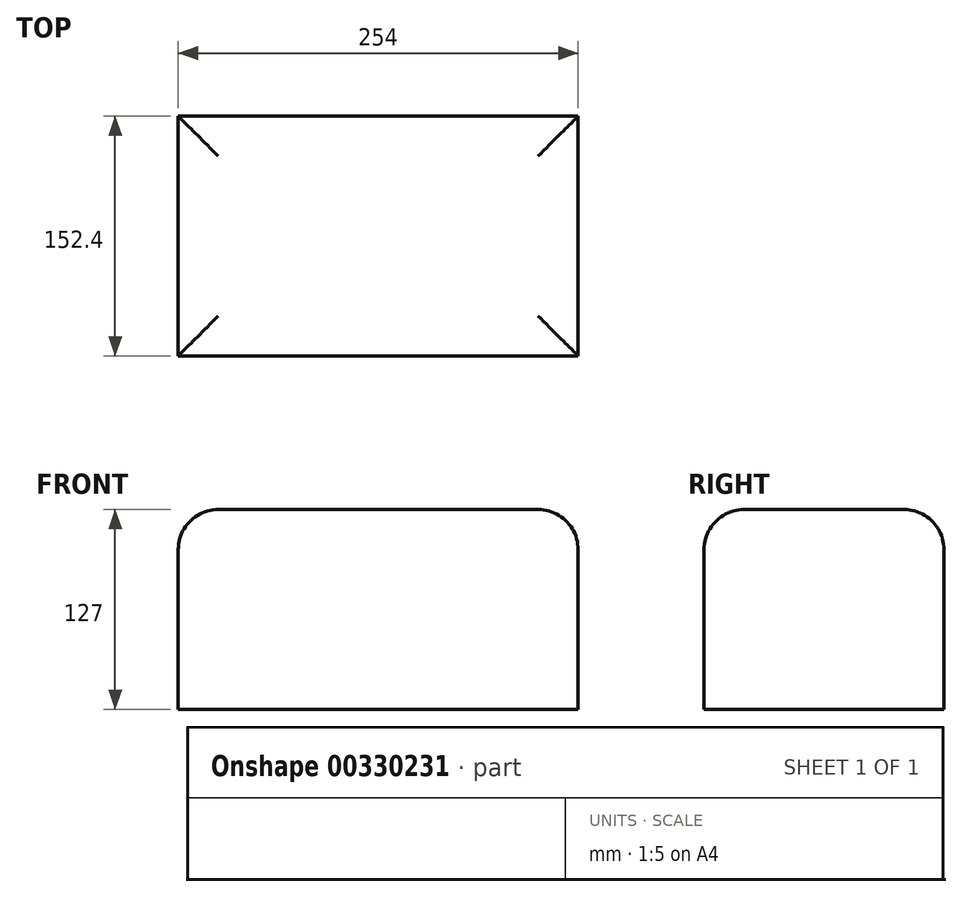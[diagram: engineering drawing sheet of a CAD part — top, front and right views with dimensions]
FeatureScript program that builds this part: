
annotation { "Feature Type Name" : "Feature", "Feature Type Description" : "" }
export const myFeature = defineFeature(function(context is Context, id is Id, definition is map)
    precondition{}
    {
        {
            var Q0;
            Q0=qCreatedBy(makeId("Top.planeOp"),FACE);
            var sketch = newSketch(context, id + "F0", { "sketchPlane" : qUnion([Q0])});
            skLineSegment(sketch, "E0.bottom", {"start": v(0, 0) * mm, "end": v(254, 0) * mm});
            skLineSegment(sketch, "E0.top", {"start": v(0, 152.4) * mm, "end": v(254, 152.4) * mm});
            skLineSegment(sketch, "E0.left", {"start": v(0, 0) * mm, "end": v(0, 152.4) * mm});
            skLineSegment(sketch, "E0.right", {"start": v(254, 0) * mm, "end": v(254, 152.4) * mm});
            skSolve(sketch);
        }
        {
            var Q0;
            Q0=makeQuery(id+"F0.imprint","IMPRINT",FACE,{"disambiguationData":[TD([[makeQuery(id+"F0.imprint","IMPRINT",EDGE,{"derivedFrom":sQuery(id+"F0.wireOp",EDGE,"E0.bottom")}),1.0]])]});
            extrude(context, id + "F1", {"entities" : qUnion([Q0]), "depth" : 127 * mm});
        }
        {
            var Q0;
            Q0=makeQuery(id+"F1.opExtrude","CAP_FACE",FACE,{"disambiguationData":[OSD([sQuery(id+"F0.wireOp",EDGE,"E0.bottom"),sQuery(id+"F0.wireOp",EDGE,"E0.top"),sQuery(id+"F0.wireOp",EDGE,"E0.left"),sQuery(id+"F0.wireOp",EDGE,"E0.right")])],"isStart":false});
            fillet(context, id + "F2", {"entities" : qUnion([Q0]), "radius" : 25.4 * mm, "tangentPropagation" : true, "allowEdgeOverflow" : false});
        }
    });
